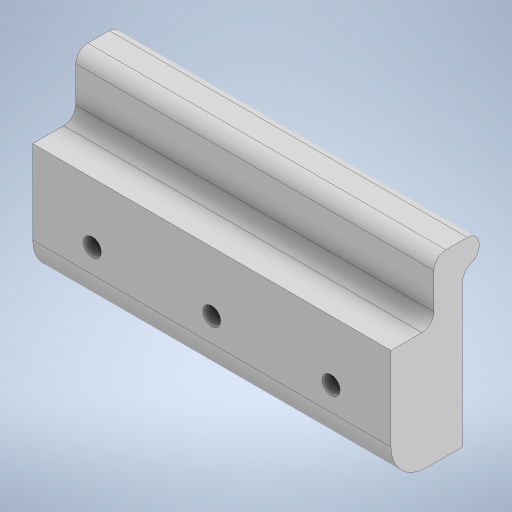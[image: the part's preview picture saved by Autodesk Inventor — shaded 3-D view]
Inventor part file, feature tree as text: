
AUTODESK INVENTOR PART (.ipt)
format: ipt  version: 2024.2 (Build 282272000, 272)  size: 265,728 bytes
history: native  units: mm
features: extrude x2, fillet x2, sketch x2, other x1, projected_geometry x1
ambient origin geometry x8: Origin, YZ Plane, XZ Plane, XY Plane, X Axis, Y Axis, Z Axis, Center Point
bodies: Body1 (feature_tree)
feature tree (8):
  other  "Bryła1"
  extrude  "Wyciągnięcie proste1"  Depth=2.4mm
  fillet  "Zaokrąglenie1"  Radius=3.8mm
  fillet  "Zaokrąglenie2"  Radius=2.0mm
  extrude  "Wyciągnięcie proste5"  Depth=3.6mm
  sketch  "Szkic1"
  sketch  "Szkic4"
  projected_geometry  "Pętla rzutowana4"
